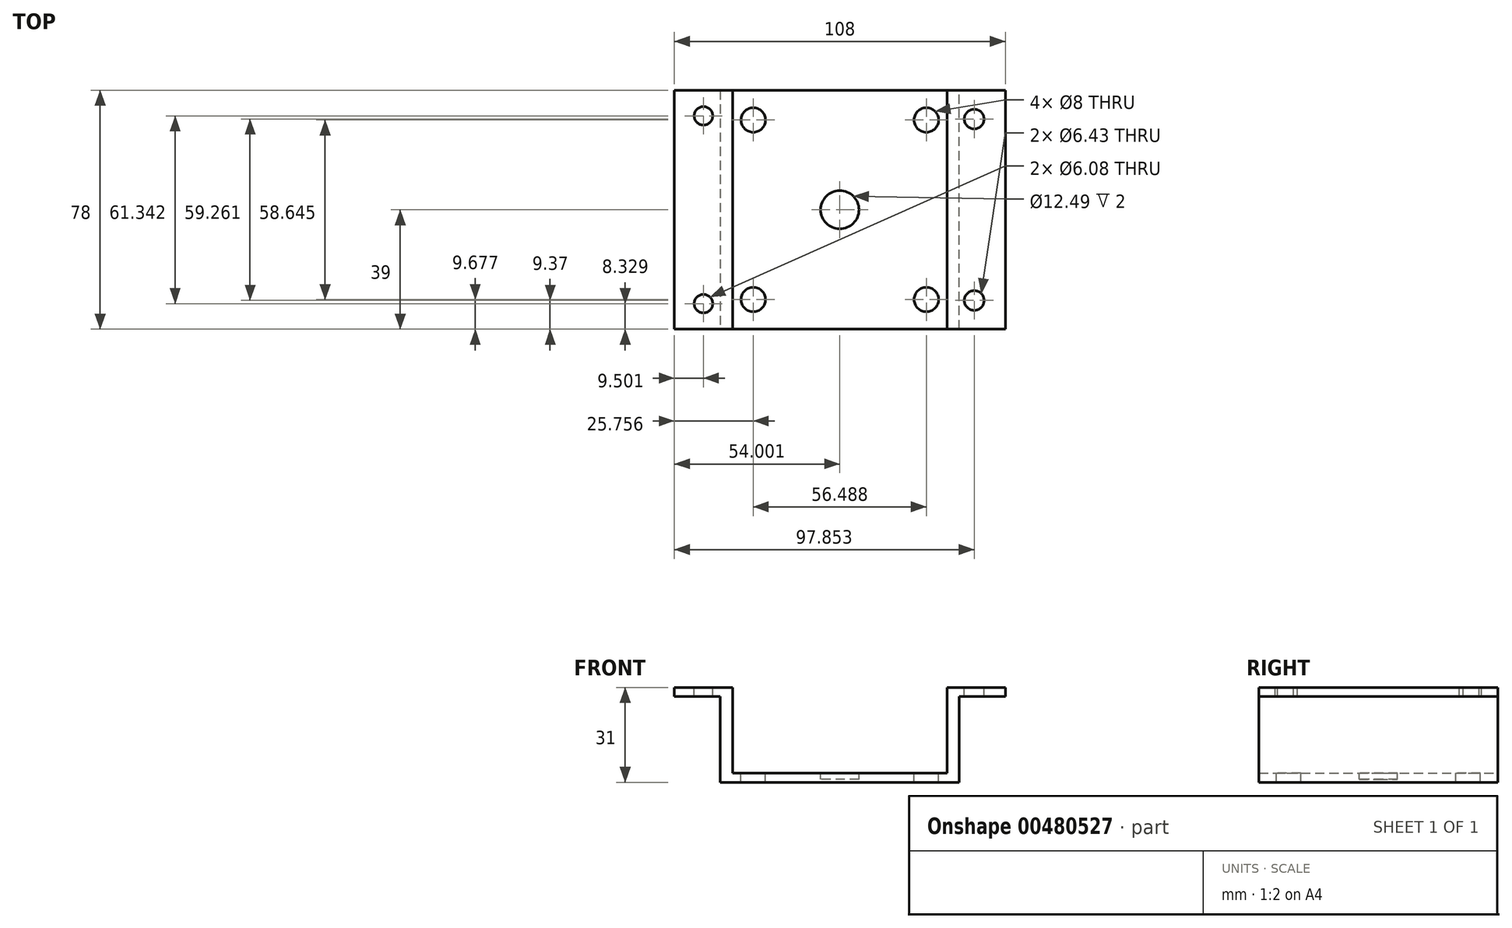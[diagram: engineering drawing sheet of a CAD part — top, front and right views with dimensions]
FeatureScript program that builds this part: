
annotation { "Feature Type Name" : "Feature", "Feature Type Description" : "" }
export const myFeature = defineFeature(function(context is Context, id is Id, definition is map)
    precondition{}
    {
        {
            var Q0;
            Q0=qCreatedBy(makeId("Front.planeOp"),FACE);
            var sketch = newSketch(context, id + "F0", { "sketchPlane" : qUnion([Q0])});
            skLineSegment(sketch, "E0.bottom", {"start": v(-34.97, 0) * mm, "end": v(43.03, 0) * mm});
            skLineSegment(sketch, "E0.top", {"start": v(-34.97, -3) * mm, "end": v(43.03, -3) * mm});
            skLineSegment(sketch, "E0.left", {"start": v(-34.97, 0) * mm, "end": v(-34.97, -3) * mm});
            skLineSegment(sketch, "E0.right", {"start": v(43.03, 0) * mm, "end": v(43.03, -3) * mm});
            skSolve(sketch);
        }
        {
            var Q0;
            Q0=makeQuery(id+"F0.imprint","IMPRINT",FACE,{"disambiguationData":[TD([[makeQuery(id+"F0.imprint","IMPRINT",EDGE,{"derivedFrom":sQuery(id+"F0.wireOp",EDGE,"E0.bottom")}),-1.0]])]});
            extrude(context, id + "F1", {"entities" : qUnion([Q0]), "depth" : 78 * mm});
        }
        {
            var Q0;
            Q0=makeQuery(id+"F1.opExtrude","SWEPT_FACE",FACE,{"disambiguationData":[OSD([sQuery(id+"F0.wireOp",EDGE,"E0.bottom")])]});
            var sketch = newSketch(context, id + "F2", { "sketchPlane" : qUnion([Q0])});
            skLineSegment(sketch, "E1.bottom", {"start": v(-34.97, -78) * mm, "end": v(-30.97, -78) * mm});
            skLineSegment(sketch, "E1.top", {"start": v(-34.97, 0) * mm, "end": v(-30.97, 0) * mm});
            skLineSegment(sketch, "E1.left", {"start": v(-34.97, -78) * mm, "end": v(-34.97, 0) * mm});
            skLineSegment(sketch, "E1.right", {"start": v(-30.97, -78) * mm, "end": v(-30.97, 0) * mm});
            skSolve(sketch);
        }
        {
            var Q0;
            Q0=makeQuery(id+"F2.imprint","IMPRINT",FACE,{"disambiguationData":[TD([[makeQuery(id+"F2.imprint","IMPRINT",EDGE,{"derivedFrom":sQuery(id+"F2.wireOp",EDGE,"E1.bottom")}),1.0]])]});
            extrude(context, id + "F3", {"entities" : qUnion([Q0]), "operationType" : NewBodyOperationType.ADD, "depth" : 28 * mm});
        }
        {
            var Q0;
            Q0=makeQuery(id+"F1.opExtrude","SWEPT_FACE",FACE,{"disambiguationData":[OSD([sQuery(id+"F0.wireOp",EDGE,"E0.bottom")])]});
            var sketch = newSketch(context, id + "F4", { "sketchPlane" : qUnion([Q0])});
            skLineSegment(sketch, "E2.bottom", {"start": v(43.03, -78) * mm, "end": v(39.03, -78) * mm});
            skLineSegment(sketch, "E2.top", {"start": v(43.03, 0) * mm, "end": v(39.03, 0) * mm});
            skLineSegment(sketch, "E2.left", {"start": v(43.03, -78) * mm, "end": v(43.03, 0) * mm});
            skLineSegment(sketch, "E2.right", {"start": v(39.03, -78) * mm, "end": v(39.03, 0) * mm});
            skSolve(sketch);
        }
        {
            var Q0;
            Q0 = qSketchRegion(id + "F4", true);
            extrude(context, id + "F5", {"entities" : qUnion([Q0]), "operationType" : NewBodyOperationType.ADD, "depth" : 28 * mm});
        }
        {
            var Q0;
            Q0=makeQuery(id+"F3.boolean.opBoolean","MERGE",FACE,{"derivedFrom":[makeQuery(id+"F1.opExtrude","SWEPT_FACE",FACE,{"disambiguationData":[OSD([sQuery(id+"F0.wireOp",EDGE,"E0.left")])]}),makeQuery(id+"F3.opExtrude","SWEPT_FACE",FACE,{"disambiguationData":[OSD([sQuery(id+"F2.wireOp",EDGE,"E1.left")])]})]});
            var sketch = newSketch(context, id + "F6", { "sketchPlane" : qUnion([Q0])});
            skLineSegment(sketch, "E3.bottom", {"start": v(0, 25) * mm, "end": v(78, 25) * mm});
            skLineSegment(sketch, "E3.top", {"start": v(0, 22) * mm, "end": v(78, 22) * mm});
            skLineSegment(sketch, "E3.left", {"start": v(0, 25) * mm, "end": v(0, 22) * mm});
            skLineSegment(sketch, "E3.right", {"start": v(78, 25) * mm, "end": v(78, 22) * mm});
            skSolve(sketch);
        }
        {
            var Q0;
            Q0=makeQuery(id+"F6.imprint","IMPRINT",FACE,{"disambiguationData":[TD([[makeQuery(id+"F6.imprint","IMPRINT",EDGE,{"derivedFrom":sQuery(id+"F6.wireOp",EDGE,"E3.bottom")}),1.0]])]});
            extrude(context, id + "F7", {"entities" : qUnion([Q0]), "operationType" : NewBodyOperationType.ADD, "depth" : 15 * mm});
        }
        {
            var Q0;
            Q0=makeQuery(id+"F5.boolean.opBoolean","MERGE",FACE,{"derivedFrom":[makeQuery(id+"F1.opExtrude","SWEPT_FACE",FACE,{"disambiguationData":[OSD([sQuery(id+"F0.wireOp",EDGE,"E0.right")])]}),makeQuery(id+"F5.opExtrude","SWEPT_FACE",FACE,{"disambiguationData":[OSD([sQuery(id+"F4.wireOp",EDGE,"E2.left")])]})]});
            var sketch = newSketch(context, id + "F8", { "sketchPlane" : qUnion([Q0])});
            skLineSegment(sketch, "E4.bottom", {"start": v(-78, 28) * mm, "end": v(0, 28) * mm});
            skLineSegment(sketch, "E4.top", {"start": v(-78, 25) * mm, "end": v(0, 25) * mm});
            skLineSegment(sketch, "E4.left", {"start": v(-78, 28) * mm, "end": v(-78, 25) * mm});
            skLineSegment(sketch, "E4.right", {"start": v(0, 28) * mm, "end": v(0, 25) * mm});
            skSolve(sketch);
        }
        {
            var Q0;
            Q0 = qSketchRegion(id + "F8", true);
            extrude(context, id + "F9", {"entities" : qUnion([Q0]), "operationType" : NewBodyOperationType.ADD, "depth" : 15 * mm});
        }
        {
            var Q0;
            Q0=makeQuery(id+"F1.opExtrude","SWEPT_FACE",FACE,{"disambiguationData":[OSD([sQuery(id+"F0.wireOp",EDGE,"E0.bottom")])]});
            var sketch = newSketch(context, id + "F10", { "sketchPlane" : qUnion([Q0])});
            skLineSegment(sketch, "E5", {"start": v(4.03, 0) * mm, "end": v(4.03, -78) * mm, "construction": true});
            skLineSegment(sketch, "E6", {"start": v(39.03, -39) * mm, "end": v(-30.97, -39) * mm, "construction": true});
            skCircle(sketch, "E7", {"center": v(4.03, -39) * mm, "radius": 6.25 * mm});
            skSolve(sketch);
        }
        {
            var Q0;
            Q0=makeQuery(id+"F1.opExtrude","SWEPT_FACE",FACE,{"disambiguationData":[OSD([sQuery(id+"F0.wireOp",EDGE,"E0.bottom")])]});
            var sketch = newSketch(context, id + "F11", { "sketchPlane" : qUnion([Q0])});
            skLineSegment(sketch, "E8", {"start": v(4.03, 0) * mm, "end": v(4.03, -78) * mm, "construction": true});
            skLineSegment(sketch, "E9", {"start": v(39.03, -39) * mm, "end": v(-30.97, -39) * mm, "construction": true});
            skCircle(sketch, "E10", {"center": v(-24.21, -9.68) * mm, "radius": 4 * mm});
            skCircle(sketch, "E11.MirrorC", {"center": v(32.27, -9.68) * mm, "radius": 4 * mm});
            skLineSegment(sketch, "E12.MirrorCS", {"start": v(-30.97, -39) * mm, "end": v(39.03, -39) * mm, "construction": true});
            skCircle(sketch, "E13.MirrorC", {"center": v(-24.21, -68.32) * mm, "radius": 4 * mm});
            skCircle(sketch, "E14.MirrorC", {"center": v(32.27, -68.32) * mm, "radius": 4 * mm});
            skSolve(sketch);
        }
        {
            var Q0;
            Q0=makeQuery(id+"F9.boolean.opBoolean","MERGE",FACE,{"derivedFrom":[makeQuery(id+"F5.opExtrude","CAP_FACE",FACE,{"disambiguationData":[OSD([sQuery(id+"F4.wireOp",EDGE,"E2.bottom"),sQuery(id+"F4.wireOp",EDGE,"E2.top"),sQuery(id+"F4.wireOp",EDGE,"E2.left"),sQuery(id+"F4.wireOp",EDGE,"E2.right")])],"isStart":false}),makeQuery(id+"F9.opExtrude","SWEPT_FACE",FACE,{"disambiguationData":[OSD([sQuery(id+"F8.wireOp",EDGE,"E4.bottom")])]})]});
            var sketch = newSketch(context, id + "F12", { "sketchPlane" : qUnion([Q0])});
            skLineSegment(sketch, "E15", {"start": v(58.03, -39) * mm, "end": v(39.03, -39) * mm, "construction": true});
            skCircle(sketch, "E16", {"center": v(47.88, -9.37) * mm, "radius": 3.22 * mm});
            skCircle(sketch, "E17.MirrorC", {"center": v(47.88, -68.63) * mm, "radius": 3.22 * mm});
            skSolve(sketch);
        }
        {
            var Q0;
            Q0 = qSketchRegion(id + "F12", true);
            extrude(context, id + "F13", {"entities" : qUnion([Q0]), "operationType" : NewBodyOperationType.REMOVE, "oppositeDirection" : true, "depth" : 22.5 * mm});
        }
        {
            var Q0;
            {var subQ0=sQuery(id+"F2.wireOp",EDGE,"E1.left");Q0=makeQuery(id+"F7.boolean.opBoolean","MERGE",FACE,{"derivedFrom":[makeQuery(id+"F3.opExtrude","CAP_FACE",FACE,{"disambiguationData":[OSD([sQuery(id+"F2.wireOp",EDGE,"E1.bottom"),sQuery(id+"F2.wireOp",EDGE,"E1.top"),subQ0,sQuery(id+"F2.wireOp",EDGE,"E1.right")])],"isStart":false}),makeQuery(id+"F7.opExtrude","SWEPT_FACE",FACE,{"disambiguationData":[OSD([subQ0])]})]});}
            var sketch = newSketch(context, id + "F14", { "sketchPlane" : qUnion([Q0])});
            skLineSegment(sketch, "E18", {"start": v(-49.97, -39) * mm, "end": v(-30.97, -39) * mm, "construction": true});
            skCircle(sketch, "E19", {"center": v(-40.47, -8.33) * mm, "radius": 3.04 * mm});
            skPoint(sketch, "E19.centerSnap0", {"position": v(-40.47, 0) * mm});
            skCircle(sketch, "E20.MirrorC", {"center": v(-40.47, -69.67) * mm, "radius": 3.04 * mm});
            skSolve(sketch);
        }
        {
            var Q0;
            Q0 = qSketchRegion(id + "F14", true);
            extrude(context, id + "F15", {"entities" : qUnion([Q0]), "operationType" : NewBodyOperationType.REMOVE, "oppositeDirection" : true, "depth" : 18.4 * mm});
        }
        {
            var Q0;
            Q0=makeQuery(id+"F10.imprint","IMPRINT",FACE,{"disambiguationData":[TD([[makeQuery(id+"F10.imprint","IMPRINT",EDGE,{"derivedFrom":sQuery(id+"F10.wireOp",EDGE,"E7")}),1.0]])]});
            extrude(context, id + "F16", {"entities" : qUnion([Q0]), "operationType" : NewBodyOperationType.REMOVE, "oppositeDirection" : true, "depth" : 2 * mm});
        }
        {
            var Q0;
            Q0 = qSketchRegion(id + "F11", true);
            extrude(context, id + "F17", {"entities" : qUnion([Q0]), "operationType" : NewBodyOperationType.REMOVE, "oppositeDirection" : true, "depth" : 12.6 * mm});
        }
    });
